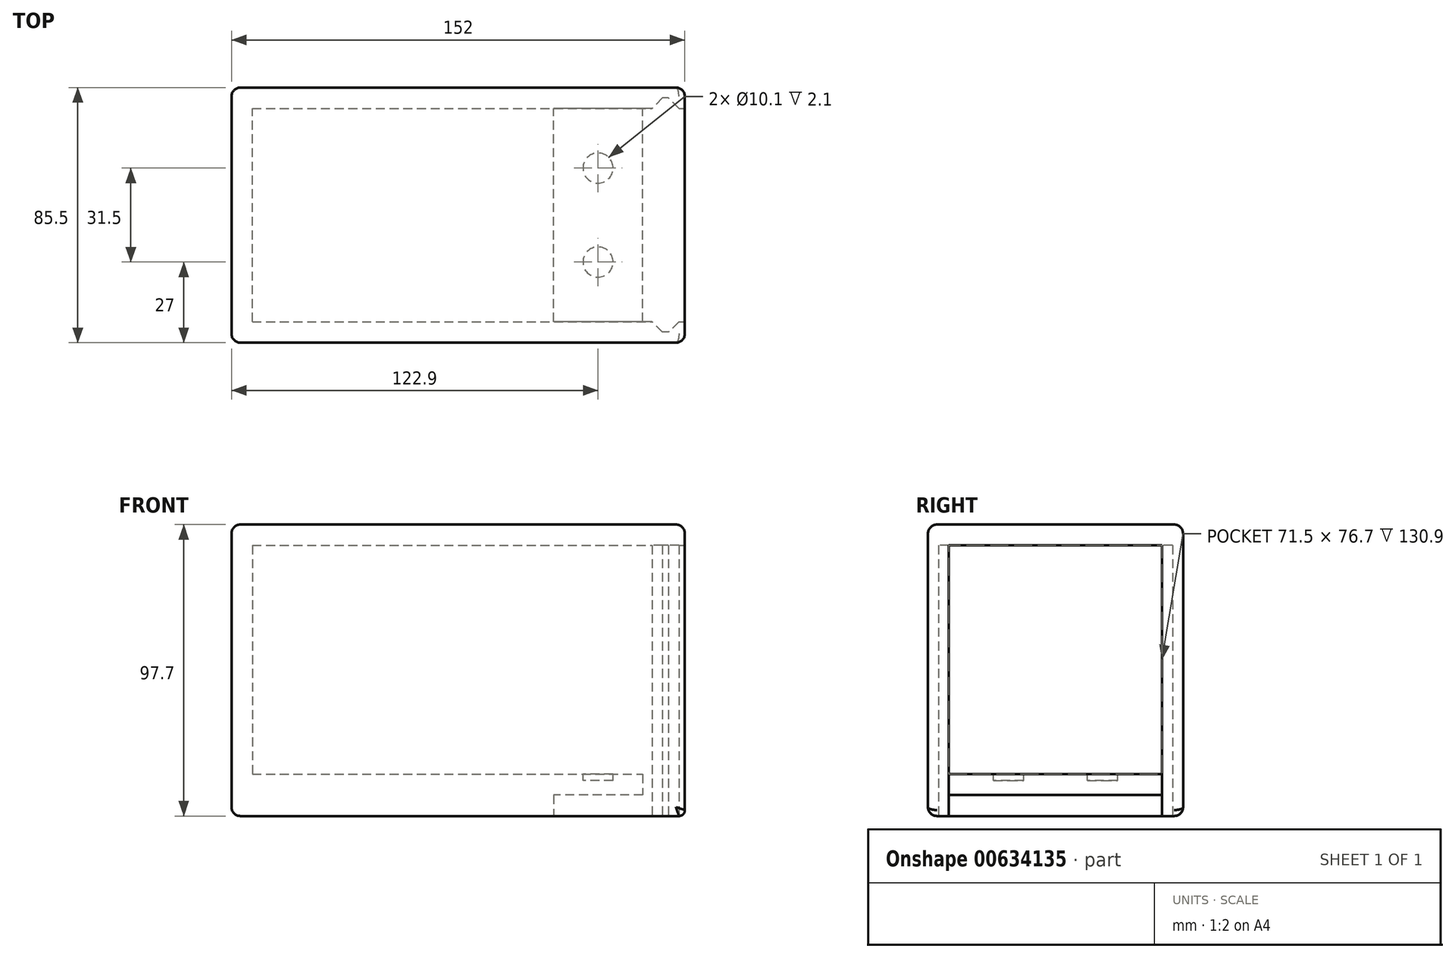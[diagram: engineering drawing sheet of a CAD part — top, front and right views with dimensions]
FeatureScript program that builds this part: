
annotation { "Feature Type Name" : "Feature", "Feature Type Description" : "" }
export const myFeature = defineFeature(function(context is Context, id is Id, definition is map)
    precondition{}
    {
        {
            var Q0;
            Q0=qCreatedBy(makeId("Top.planeOp"),FACE);
            var sketch = newSketch(context, id + "F0", { "sketchPlane" : qUnion([Q0])});
            skLineSegment(sketch, "E0.bottom", {"start": v(-76, 42.75) * mm, "end": v(76, 42.75) * mm});
            skLineSegment(sketch, "E0.top", {"start": v(-76, -42.75) * mm, "end": v(76, -42.75) * mm});
            skLineSegment(sketch, "E0.left", {"start": v(-76, 42.75) * mm, "end": v(-76, -42.75) * mm});
            skLineSegment(sketch, "E0.right", {"start": v(76, 42.75) * mm, "end": v(76, -42.75) * mm});
            skSolve(sketch);
        }
        {
            var Q0;
            Q0=makeQuery(id+"F0.imprint","IMPRINT",FACE,{"disambiguationData":[TD([[makeQuery(id+"F0.imprint","IMPRINT",EDGE,{"derivedFrom":sQuery(id+"F0.wireOp",EDGE,"E0.bottom")}),-1.0]])]});
            extrude(context, id + "F1", {"entities" : qUnion([Q0]), "depth" : 97.7 * mm, "offsetDistance" : 25 * mm});
        }
        {
            var Q0;
            Q0=makeQuery(id+"F1.opExtrude","SWEPT_FACE",FACE,{"disambiguationData":[OSD([sQuery(id+"F0.wireOp",EDGE,"E0.right")])]});
            var sketch = newSketch(context, id + "F2", { "sketchPlane" : qUnion([Q0])});
            skLineSegment(sketch, "E1.bottom", {"start": v(-35.75, 90.7) * mm, "end": v(35.75, 90.7) * mm});
            skLineSegment(sketch, "E1.top", {"start": v(-35.75, 14) * mm, "end": v(35.75, 14) * mm});
            skLineSegment(sketch, "E1.left", {"start": v(-35.75, 90.7) * mm, "end": v(-35.75, 14) * mm});
            skLineSegment(sketch, "E1.right", {"start": v(35.75, 90.7) * mm, "end": v(35.75, 14) * mm});
            skSolve(sketch);
        }
        {
            var Q0;
            Q0=makeQuery(id+"F2.imprint","IMPRINT",FACE,{"disambiguationData":[TD([[makeQuery(id+"F2.imprint","IMPRINT",EDGE,{"derivedFrom":sQuery(id+"F2.wireOp",EDGE,"E1.bottom")}),-1.0]])]});
            extrude(context, id + "F3", {"entities" : qUnion([Q0]), "operationType" : NewBodyOperationType.REMOVE, "oppositeDirection" : true, "depth" : 145 * mm, "offsetDistance" : 25 * mm});
        }
        {
            var Q0;
            Q0=makeQuery(id+"F1.opExtrude","CAP_FACE",FACE,{"disambiguationData":[OSD([sQuery(id+"F0.wireOp",EDGE,"E0.bottom"),sQuery(id+"F0.wireOp",EDGE,"E0.top"),sQuery(id+"F0.wireOp",EDGE,"E0.left"),sQuery(id+"F0.wireOp",EDGE,"E0.right")])],"isStart":true});
            var sketch = newSketch(context, id + "F4", { "sketchPlane" : qUnion([Q0])});
            skLineSegment(sketch, "E2.bottom", {"start": v(76, 35.75) * mm, "end": v(32, 35.75) * mm});
            skLineSegment(sketch, "E2.top", {"start": v(76, -35.75) * mm, "end": v(32, -35.75) * mm});
            skLineSegment(sketch, "E2.left", {"start": v(76, 35.75) * mm, "end": v(76, -35.75) * mm});
            skLineSegment(sketch, "E2.right", {"start": v(32, 35.75) * mm, "end": v(32, -35.75) * mm});
            skSolve(sketch);
        }
        {
            var Q0;
            Q0=makeQuery(id+"F4.imprint","IMPRINT",FACE,{"disambiguationData":[TD([[makeQuery(id+"F4.imprint","IMPRINT",EDGE,{"derivedFrom":sQuery(id+"F4.wireOp",EDGE,"E2.bottom")}),1.0]])]});
            extrude(context, id + "F5", {"entities" : qUnion([Q0]), "operationType" : NewBodyOperationType.REMOVE, "oppositeDirection" : true, "depth" : 7 * mm, "offsetDistance" : 25 * mm});
        }
        {
            var Q0;
            Q0=makeQuery(id+"F5.boolean.opBoolean","COPY",FACE,{"derivedFrom":makeQuery(id+"F5.opExtrude","CAP_FACE",FACE,{"disambiguationData":[OSD([sQuery(id+"F4.wireOp",EDGE,"E2.bottom"),sQuery(id+"F4.wireOp",EDGE,"E2.top"),sQuery(id+"F4.wireOp",EDGE,"E2.left"),sQuery(id+"F4.wireOp",EDGE,"E2.right")])],"isStart":false})});
            var sketch = newSketch(context, id + "F6", { "sketchPlane" : qUnion([Q0])});
            skLineSegment(sketch, "E3.bottom", {"start": v(76, 35.75) * mm, "end": v(61.9, 35.75) * mm});
            skLineSegment(sketch, "E3.top", {"start": v(76, -35.75) * mm, "end": v(61.9, -35.75) * mm});
            skLineSegment(sketch, "E3.left", {"start": v(76, 35.75) * mm, "end": v(76, -35.75) * mm});
            skLineSegment(sketch, "E3.right", {"start": v(61.9, 35.75) * mm, "end": v(61.9, -35.75) * mm});
            skSolve(sketch);
        }
        {
            var Q0;
            Q0=makeQuery(id+"F6.imprint","IMPRINT",FACE,{"disambiguationData":[TD([[makeQuery(id+"F6.imprint","IMPRINT",EDGE,{"derivedFrom":sQuery(id+"F6.wireOp",EDGE,"E3.bottom")}),1.0]])]});
            extrude(context, id + "F7", {"entities" : qUnion([Q0]), "operationType" : NewBodyOperationType.REMOVE, "oppositeDirection" : true, "depth" : 7 * mm, "offsetDistance" : 25 * mm});
        }
        {
            var Q0;
            Q0=makeQuery(id+"F1.opExtrude","CAP_FACE",FACE,{"disambiguationData":[OSD([sQuery(id+"F0.wireOp",EDGE,"E0.bottom"),sQuery(id+"F0.wireOp",EDGE,"E0.top"),sQuery(id+"F0.wireOp",EDGE,"E0.left"),sQuery(id+"F0.wireOp",EDGE,"E0.right")])],"isStart":true});
            var sketch = newSketch(context, id + "F8", { "sketchPlane" : qUnion([Q0])});
            skLineSegment(sketch, "E4", {"start": v(74, 35.75) * mm, "end": v(70.5, 39.25) * mm});
            skLineSegment(sketch, "E5", {"start": v(70.5, 39.25) * mm, "end": v(68.5, 39.25) * mm});
            skLineSegment(sketch, "E6", {"start": v(68.5, 39.25) * mm, "end": v(65, 35.75) * mm});
            skLineSegment(sketch, "E7", {"start": v(65, 35.75) * mm, "end": v(74, 35.75) * mm});
            skLineSegment(sketch, "E8", {"start": v(74, -35.75) * mm, "end": v(70.5, -39.25) * mm});
            skLineSegment(sketch, "E9", {"start": v(70.5, -39.25) * mm, "end": v(68.5, -39.25) * mm});
            skLineSegment(sketch, "E10", {"start": v(68.5, -39.25) * mm, "end": v(65, -35.75) * mm});
            skLineSegment(sketch, "E11", {"start": v(65, -35.75) * mm, "end": v(74, -35.75) * mm});
            skSolve(sketch);
        }
        {
            var Q0;
            Q0=makeQuery(id+"F8.imprint","IMPRINT",FACE,{"disambiguationData":[TD([[makeQuery(id+"F8.imprint","IMPRINT",EDGE,{"derivedFrom":sQuery(id+"F8.wireOp",EDGE,"E4")}),1.0]])]});
            var Q1;
            Q1=makeQuery(id+"F8.imprint","IMPRINT",FACE,{"disambiguationData":[TD([[makeQuery(id+"F8.imprint","IMPRINT",EDGE,{"derivedFrom":sQuery(id+"F8.wireOp",EDGE,"E8")}),-1.0]])]});
            extrude(context, id + "F9", {"entities" : qUnion([Q0, Q1]), "operationType" : NewBodyOperationType.REMOVE, "oppositeDirection" : true, "depth" : 90.7 * mm, "offsetDistance" : 25 * mm});
        }
        {
            var Q0;
            Q0=makeQuery(id+"F1.opExtrude","CAP_EDGE",EDGE,{"disambiguationData":[OSD([sQuery(id+"F0.wireOp",EDGE,"E0.top")])],"isStart":true});
            var Q1;
            Q1=makeQuery(id+"F1.opExtrude","SWEPT_EDGE",EDGE,{"disambiguationData":[OSD([sQuery(id+"F0.wireOp",EDGE,"E0.top"),sQuery(id+"F0.wireOp",EDGE,"E0.right")])]});
            var Q2;
            Q2=makeQuery(id+"F1.opExtrude","SWEPT_EDGE",EDGE,{"disambiguationData":[OSD([sQuery(id+"F0.wireOp",EDGE,"E0.bottom"),sQuery(id+"F0.wireOp",EDGE,"E0.right")])]});
            var Q3;
            Q3=makeQuery(id+"F1.opExtrude","CAP_EDGE",EDGE,{"disambiguationData":[OSD([sQuery(id+"F0.wireOp",EDGE,"E0.bottom")])],"isStart":true});
            var Q4;
            Q4=makeQuery(id+"F1.opExtrude","CAP_EDGE",EDGE,{"disambiguationData":[OSD([sQuery(id+"F0.wireOp",EDGE,"E0.left")])],"isStart":true});
            var Q5;
            Q5=makeQuery(id+"F1.opExtrude","SWEPT_EDGE",EDGE,{"disambiguationData":[OSD([sQuery(id+"F0.wireOp",EDGE,"E0.bottom"),sQuery(id+"F0.wireOp",EDGE,"E0.left")])]});
            var Q6;
            Q6=makeQuery(id+"F1.opExtrude","CAP_EDGE",EDGE,{"disambiguationData":[OSD([sQuery(id+"F0.wireOp",EDGE,"E0.left")])],"isStart":false});
            var Q7;
            Q7=makeQuery(id+"F1.opExtrude","CAP_EDGE",EDGE,{"disambiguationData":[OSD([sQuery(id+"F0.wireOp",EDGE,"E0.bottom")])],"isStart":false});
            var Q8;
            Q8=makeQuery(id+"F1.opExtrude","SWEPT_EDGE",EDGE,{"disambiguationData":[OSD([sQuery(id+"F0.wireOp",EDGE,"E0.top"),sQuery(id+"F0.wireOp",EDGE,"E0.left")])]});
            var Q9;
            Q9=makeQuery(id+"F1.opExtrude","CAP_EDGE",EDGE,{"disambiguationData":[OSD([sQuery(id+"F0.wireOp",EDGE,"E0.top")])],"isStart":false});
            var Q10;
            Q10=makeQuery(id+"F1.opExtrude","CAP_EDGE",EDGE,{"disambiguationData":[OSD([sQuery(id+"F0.wireOp",EDGE,"E0.right")])],"isStart":false});
            fillet(context, id + "F10", {"entities" : qUnion([Q0, Q1, Q2, Q3, Q4, Q5, Q6, Q7, Q8, Q9, Q10]), "radius" : 3 * mm, "tangentPropagation" : true, "allowEdgeOverflow" : false});
        }
        {
            var Q0;
            {var subQ0=sQuery(id+"F0.wireOp",EDGE,"E0.bottom");var subQ1=sQuery(id+"F0.wireOp",EDGE,"E0.right");Q0=makeQuery(id+"F5.boolean.opBoolean","SPLIT",EDGE,{"disambiguationData":[TD([makeQuery(id+"F1.opExtrude","SWEPT_FACE",FACE,{"disambiguationData":[OSD([subQ0])]})])],"derivedFrom":makeQuery(id+"F1.opExtrude","CAP_EDGE",EDGE,{"disambiguationData":[OSD([subQ1])],"isStart":true})});}
            var Q1;
            {var subQ0=sQuery(id+"F0.wireOp",EDGE,"E0.right");var subQ1=sQuery(id+"F0.wireOp",EDGE,"E0.top");Q1=makeQuery(id+"F5.boolean.opBoolean","SPLIT",EDGE,{"disambiguationData":[TD([makeQuery(id+"F1.opExtrude","SWEPT_FACE",FACE,{"disambiguationData":[OSD([subQ1])]})])],"derivedFrom":makeQuery(id+"F1.opExtrude","CAP_EDGE",EDGE,{"disambiguationData":[OSD([subQ0])],"isStart":true})});}
            fillet(context, id + "F11", {"entities" : qUnion([Q0, Q1]), "radius" : 2 * mm, "tangentPropagation" : true, "allowEdgeOverflow" : false});
        }
        {
            var Q0;
            Q0=makeQuery(id+"F3.boolean.opBoolean","COPY",FACE,{"derivedFrom":makeQuery(id+"F3.opExtrude","SWEPT_FACE",FACE,{"disambiguationData":[OSD([sQuery(id+"F2.wireOp",EDGE,"E1.top")])]})});
            var sketch = newSketch(context, id + "F12", { "sketchPlane" : qUnion([Q0])});
            skCircle(sketch, "E12", {"center": v(46.9, -15.75) * mm, "radius": 5.05 * mm});
            skCircle(sketch, "E13", {"center": v(46.9, 15.75) * mm, "radius": 5.05 * mm});
            skSolve(sketch);
        }
        {
            var Q0;
            Q0=makeQuery(id+"F12.imprint","IMPRINT",FACE,{"disambiguationData":[TD([[makeQuery(id+"F12.imprint","IMPRINT",EDGE,{"derivedFrom":sQuery(id+"F12.wireOp",EDGE,"E12")}),1.0]])]});
            var Q1;
            Q1=makeQuery(id+"F12.imprint","IMPRINT",FACE,{"disambiguationData":[TD([[makeQuery(id+"F12.imprint","IMPRINT",EDGE,{"derivedFrom":sQuery(id+"F12.wireOp",EDGE,"E13")}),1.0]])]});
            extrude(context, id + "F13", {"entities" : qUnion([Q0, Q1]), "operationType" : NewBodyOperationType.REMOVE, "oppositeDirection" : true, "depth" : 2.1 * mm, "offsetDistance" : 25 * mm});
        }
    });
